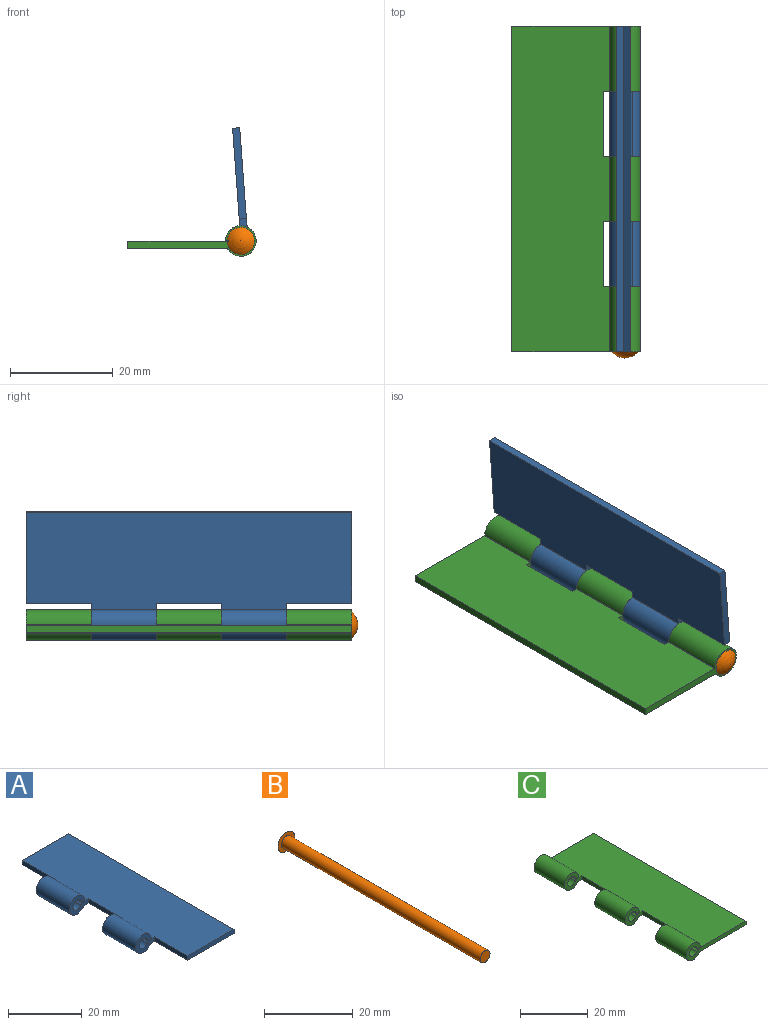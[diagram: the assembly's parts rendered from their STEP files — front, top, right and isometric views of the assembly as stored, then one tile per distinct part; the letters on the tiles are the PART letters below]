
ASSEMBLY  parts=3 mates=4
PART A: 22 faces, bbox 25x63.5x6 mm
  f0: plane 63.5x19.05mm, normal (0,0,-1), area 1160.6mm2, adj f2,f7,f12,f13,f14,f15,f16,f17
  f1: plane 63.5x19.05mm, normal (0,0,1), area 1160.6mm2, adj f2,f3,f8,f13,f14,f15,f16,f17
  f2: plane 17.76x1.4mm, normal (0,1,0), area 24.8mm2, adj f0,f1,f13,f20
  f3: cylinder r=2.05mm len=12.7mm, axis (0,-1,0), area 21.7mm2, adj f1,f4,f19,f21
  f4: cylinder r=1.61mm len=12.7mm, axis (0,-1,0), area 118.8mm2, adj f3,f5,f19,f21
  f5: plane 12.7x1.37mm, normal (0,0,-1), area 17.4mm2, adj f4,f6,f19,f21
  f6: cylinder r=2.98mm len=12.7mm, axis (0,-1,0), area 214.7mm2, adj f5,f7,f19,f21
  f7: cylinder r=0.62mm len=12.7mm, axis (0,-1,0), area 7.4mm2, adj f0,f6,f19,f21
  f8: cylinder r=2.05mm len=12.7mm, axis (0,-1,0), area 21.7mm2, adj f1,f9,f16,f18
  f9: cylinder r=1.61mm len=12.7mm, axis (0,-1,0), area 118.8mm2, adj f8,f10,f16,f18
  f10: plane 12.7x1.37mm, normal (0,0,-1), area 17.4mm2, adj f9,f11,f16,f18
  f11: cylinder r=2.98mm len=12.7mm, axis (0,-1,0), area 214.7mm2, adj f10,f12,f16,f18
  f12: cylinder r=0.62mm len=12.7mm, axis (0,-1,0), area 7.4mm2, adj f0,f11,f16,f18
  f13: plane 63.5x1.4mm, normal (1,0,0), area 88.7mm2, adj f0,f1,f2,f14
  f14: plane 17.77x1.4mm, normal (0,-1,0), area 24.8mm2, adj f0,f1,f13,f15
  f15: plane 12.7x1.4mm, normal (-1,0,0), area 17.7mm2, adj f0,f1,f14,f16
  f16: plane 7.25x5.97mm, normal (0,-1,0), area 21.4mm2, adj f0,f1,f8,f9,f10,f11,f12,f15
  f17: plane 12.7x1.4mm, normal (-1,0,0), area 17.7mm2, adj f0,f1,f18,f19
  f18: plane 7.26x5.97mm, normal (0,1,0), area 21.4mm2, adj f0,f1,f8,f9,f10,f11,f12,f17
  f19: plane 7.26x5.97mm, normal (0,-1,0), area 21.4mm2, adj f0,f1,f3,f4,f5,f6,f7,f17
  f20: plane 12.7x1.4mm, normal (-1,0,0), area 17.7mm2, adj f0,f1,f2,f21
  f21: plane 7.26x5.97mm, normal (0,1,0), area 21.4mm2, adj f0,f1,f3,f4,f5,f6,f7,f20
PART B: 4 faces, bbox 5.3x64.7x5.3 mm
  f0: cylinder r=1.59mm len=63.5mm, axis (0,-1,0), area 633.4mm2, adj f1,f2
  f1: plane 3.18x3.18mm, normal (0,-1,0), area 7.9mm2, adj f0
  f2: plane 5.34x5.34mm, normal (0,-1,0), area 14.4mm2, adj f0,f3
  f3: revolved ~5.33x5.33mm, area 26.3mm2, adj f2
PART C: 26 faces, bbox 25x63.5x6 mm
  f0: plane 63.5x19.05mm, normal (0,0,-1), area 1179.1mm2, adj f6,f11,f12,f17,f18,f19,f20,f21
  f1: plane 63.5x19.05mm, normal (0,0,1), area 1179.1mm2, adj f2,f7,f12,f13,f18,f19,f20,f21
  f2: cylinder r=2.05mm len=12.7mm, axis (0,-1,0), area 21.7mm2, adj f1,f3,f21,f24
  f3: cylinder r=1.61mm len=12.7mm, axis (0,-1,0), area 118.8mm2, adj f2,f4,f21,f24
  f4: plane 12.7x1.37mm, normal (0,0,-1), area 17.4mm2, adj f3,f5,f21,f24
  f5: cylinder r=2.98mm len=12.7mm, axis (0,-1,0), area 214.7mm2, adj f4,f6,f21,f24
  f6: cylinder r=0.62mm len=12.7mm, axis (0,-1,0), area 7.4mm2, adj f0,f5,f21,f24
  f7: cylinder r=2.05mm len=12.7mm, axis (0,-1,0), area 21.7mm2, adj f1,f8,f18,f22
  f8: cylinder r=1.61mm len=12.7mm, axis (0,-1,0), area 118.8mm2, adj f7,f9,f18,f22
  f9: plane 12.7x1.37mm, normal (0,0,-1), area 17.4mm2, adj f8,f10,f18,f22
  f10: cylinder r=2.98mm len=12.7mm, axis (0,-1,0), area 214.7mm2, adj f9,f11,f18,f22
  f11: cylinder r=0.62mm len=12.7mm, axis (0,-1,0), area 7.4mm2, adj f0,f10,f18,f22
  f12: plane 63.5x1.4mm, normal (1,0,0), area 88.7mm2, adj f0,f1,f18,f19
  f13: cylinder r=2.05mm len=12.7mm, axis (0,-1,0), area 21.7mm2, adj f1,f14,f19,f25
  f14: cylinder r=1.61mm len=12.7mm, axis (0,-1,0), area 118.8mm2, adj f13,f15,f19,f25
  f15: plane 12.7x1.37mm, normal (0,0,-1), area 17.4mm2, adj f14,f16,f19,f25
  f16: cylinder r=2.98mm len=12.7mm, axis (0,-1,0), area 214.7mm2, adj f15,f17,f19,f25
  f17: cylinder r=0.62mm len=12.7mm, axis (0,-1,0), area 7.4mm2, adj f0,f16,f19,f25
  f18: plane 25.02x5.97mm, normal (0,1,0), area 46.2mm2, adj f0,f1,f7,f8,f9,f10,f11,f12
  f19: plane 25.02x5.97mm, normal (0,-1,0), area 46.2mm2, adj f0,f1,f12,f13,f14,f15,f16,f17
  f20: plane 12.7x1.4mm, normal (-1,0,0), area 17.7mm2, adj f0,f1,f21,f22
  f21: plane 7.15x5.97mm, normal (0,1,0), area 21.3mm2, adj f0,f1,f2,f3,f4,f5,f6,f20
  f22: plane 7.15x5.97mm, normal (0,-1,0), area 21.3mm2, adj f0,f1,f7,f8,f9,f10,f11,f20
  f23: plane 12.7x1.4mm, normal (-1,0,0), area 17.7mm2, adj f0,f1,f24,f25
  f24: plane 7.19x5.97mm, normal (0,-1,0), area 21.3mm2, adj f0,f1,f2,f3,f4,f5,f6,f23
  f25: plane 7.19x5.97mm, normal (0,1,0), area 21.3mm2, adj f0,f1,f13,f14,f15,f16,f17,f23
PLACE A rot(axis=(0,-1,0),94.2deg) t=(-14.71,-33.58,48.18)mm
PLACE B rot(axis=(-1,0,-0.02),180deg) t=(-15.89,29.92,45.1)mm
PLACE C rot(axis=(0,0,-1),180deg) t=(-18.87,29.92,43.69)mm fixed
MATE cylindrical B.f0 <-> C.f3  axis (0,1,0) through (-15.89,-1.83,45.1)mm
MATE planar A.f4 <-> C.f22  axis (0,-1,0) through (-15.89,-20.88,45.1)mm
MATE planar C.f18 <-> B.f0  axis (0,-1,0) through (-23.08,-33.58,44.67)mm
MATE cylindrical B.f0 <-> A.f4  axis (0,1,0) through (-15.89,-1.83,45.1)mm
